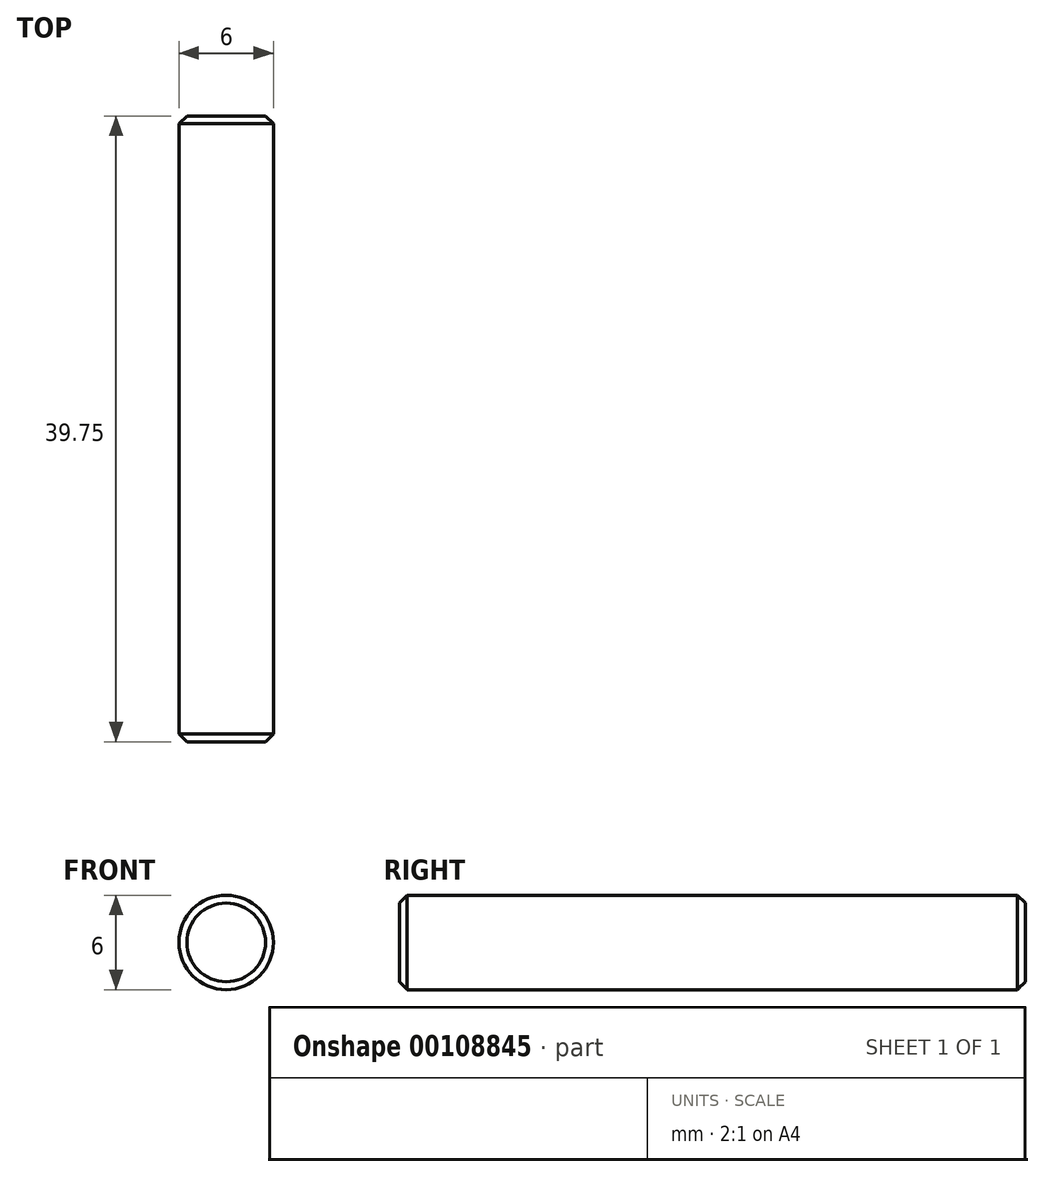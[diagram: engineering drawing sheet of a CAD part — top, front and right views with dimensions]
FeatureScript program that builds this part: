
annotation { "Feature Type Name" : "Feature", "Feature Type Description" : "" }
export const myFeature = defineFeature(function(context is Context, id is Id, definition is map)
    precondition{}
    {
        {
            var Q0;
            Q0=qCreatedBy(makeId("Front.planeOp"),FACE);
            var sketch = newSketch(context, id + "F0", { "sketchPlane" : qUnion([Q0])});
            skCircle(sketch, "E0", {"center": v(0, 0) * mm, "radius": 3 * mm});
            skSolve(sketch);
        }
        {
            var Q0;
            Q0 = qSketchRegion(id + "F0", true);
            extrude(context, id + "F1", {"entities" : qUnion([Q0]), "depth" : 39.75 * mm});
        }
        {
            var Q0;
            Q0=makeQuery(id+"F1.opExtrude","CAP_EDGE",EDGE,{"disambiguationData":[OSD([sQuery(id+"F0.wireOp",EDGE,"E0")])],"isStart":false});
            var Q1;
            Q1=makeQuery(id+"F1.opExtrude","CAP_EDGE",EDGE,{"disambiguationData":[OSD([sQuery(id+"F0.wireOp",EDGE,"E0")])],"isStart":true});
            chamfer(context, id + "F2", {"entities" : qUnion([Q0, Q1]), "width" : 0.5 * mm});
        }
    });
